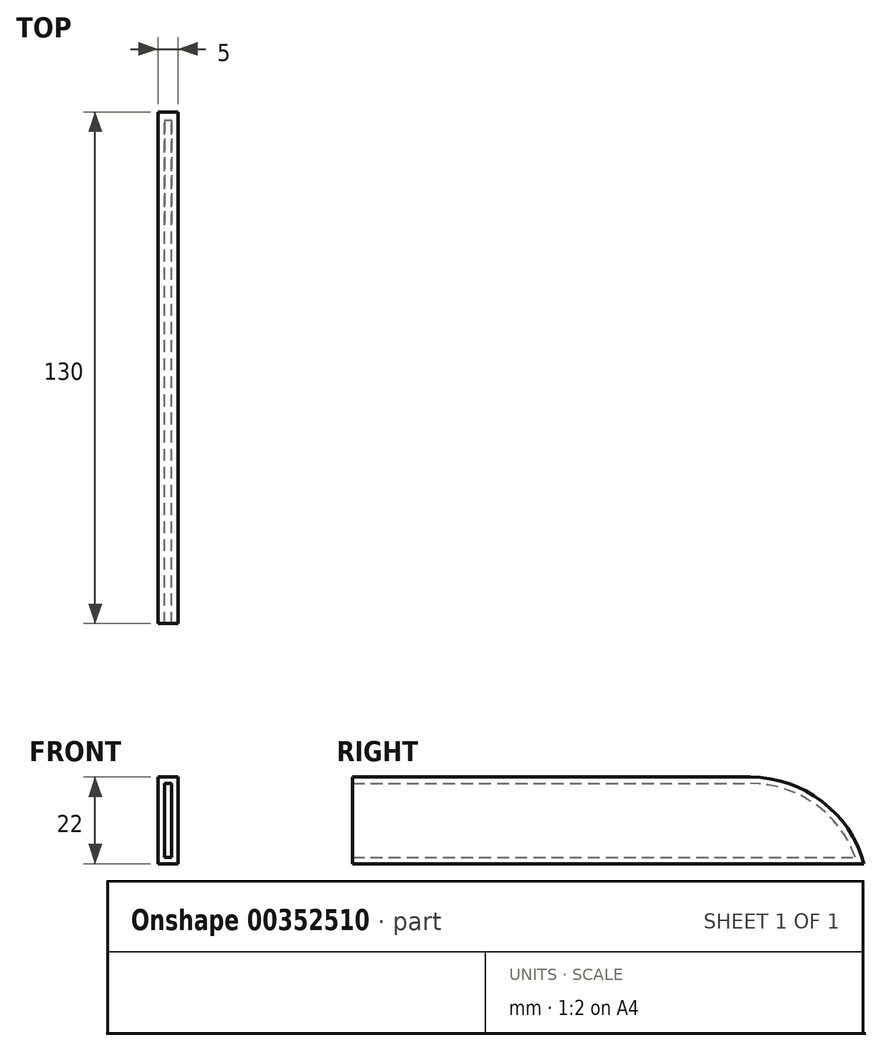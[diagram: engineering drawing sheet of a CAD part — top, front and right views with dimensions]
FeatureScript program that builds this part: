
annotation { "Feature Type Name" : "Feature", "Feature Type Description" : "" }
export const myFeature = defineFeature(function(context is Context, id is Id, definition is map)
    precondition{}
    {
        {
            var Q0;
            Q0=qCreatedBy(makeId("Right.planeOp"),FACE);
            var sketch = newSketch(context, id + "F0", { "sketchPlane" : qUnion([Q0])});
            skLineSegment(sketch, "E0", {"start": v(-65.37, 41.15) * mm, "end": v(-65.37, 19.15) * mm});
            skLineSegment(sketch, "E1", {"start": v(-65.37, 19.15) * mm, "end": v(64.63, 19.15) * mm});
            skLineSegment(sketch, "E2", {"start": v(64.63, 19.15) * mm, "end": v(64.63, 41.15) * mm});
            skLineSegment(sketch, "E3", {"start": v(-65.37, 41.15) * mm, "end": v(64.63, 41.15) * mm});
            skSolve(sketch);
        }
        {
            var Q0;
            Q0=makeQuery(id+"F0.imprint","IMPRINT",FACE,{"disambiguationData":[TD([[makeQuery(id+"F0.imprint","IMPRINT",EDGE,{"derivedFrom":sQuery(id+"F0.wireOp",EDGE,"E0")}),1.0]])]});
            extrude(context, id + "F1", {"entities" : qUnion([Q0]), "depth" : 5 * mm});
        }
        {
            var Q0;
            Q0=makeQuery(id+"F1.opExtrude","SWEPT_EDGE",EDGE,{"disambiguationData":[OSD([sQuery(id+"F0.wireOp",EDGE,"E2"),sQuery(id+"F0.wireOp",EDGE,"E3")])]});
            fillet(context, id + "F2", {"entities" : qUnion([Q0]), "radius" : 30 * mm, "tangentPropagation" : true, "allowEdgeOverflow" : false});
        }
        {
            var Q0;
            Q0=makeQuery(id+"F1.opExtrude","SWEPT_FACE",FACE,{"disambiguationData":[OSD([sQuery(id+"F0.wireOp",EDGE,"E0")])]});
            shell(context, id + "F3", {"entities" : qUnion([Q0]), "thickness" : 1.62 * mm});
        }
    });
